# Revit family: Spec Equip_ToiletRollHolder_Argent_Mondrian Neu RH
name_source: partatom
category: Specialty Equipment
revit_build: Autodesk Revit 2016 (Build: 20150220_1215(x64)
units: mm (PartAtom-declared; Revit-internal decimal feet)

## family parameters
Always vertical = Yes
Cut with Voids When Loaded = Yes
OmniClass Number = 23.40.20.21
OmniClass Title = Toilet and Bath Specialties
Part Type = Normal
Room Calculation Point = No
Round Connector Dimension = Use Diameter
Shared = No
Work Plane-Based = No

## types (1)
- Right Hand Faced - Chrome
    Body Material = z_Argent_Chrome
    CW Connection = No
    CWFU = 0
    Cost = 0 $
    Description = Mondrian Neu RH Toilet Roll Holder
    HW Connection = No
    HWFU = 0
    Manufacturer = Argent
    Manufacturer_Overall Depth = 80 mm
    Manufacturer_Overall Height = 40 mm
    Manufacturer_Overall Width = 149 mm
    Manufacturer_Spec Code = AR93686R
    Manufacturer_URL__Product Specific = https://www.argentaust.com.au
    Model = AR93686R
    ModifiedIssue_ANZRS = 20190503 $
    Type Comments = Right Hand Faced - Chrome finish
    URL = https://www.argentaust.com.au
    Vent Connection = No
    WFU = 0
    Waste Connection = No

## geometry (parser evidence)
native form markers: Sweep x2
no freeform markers — native parametric forms only
